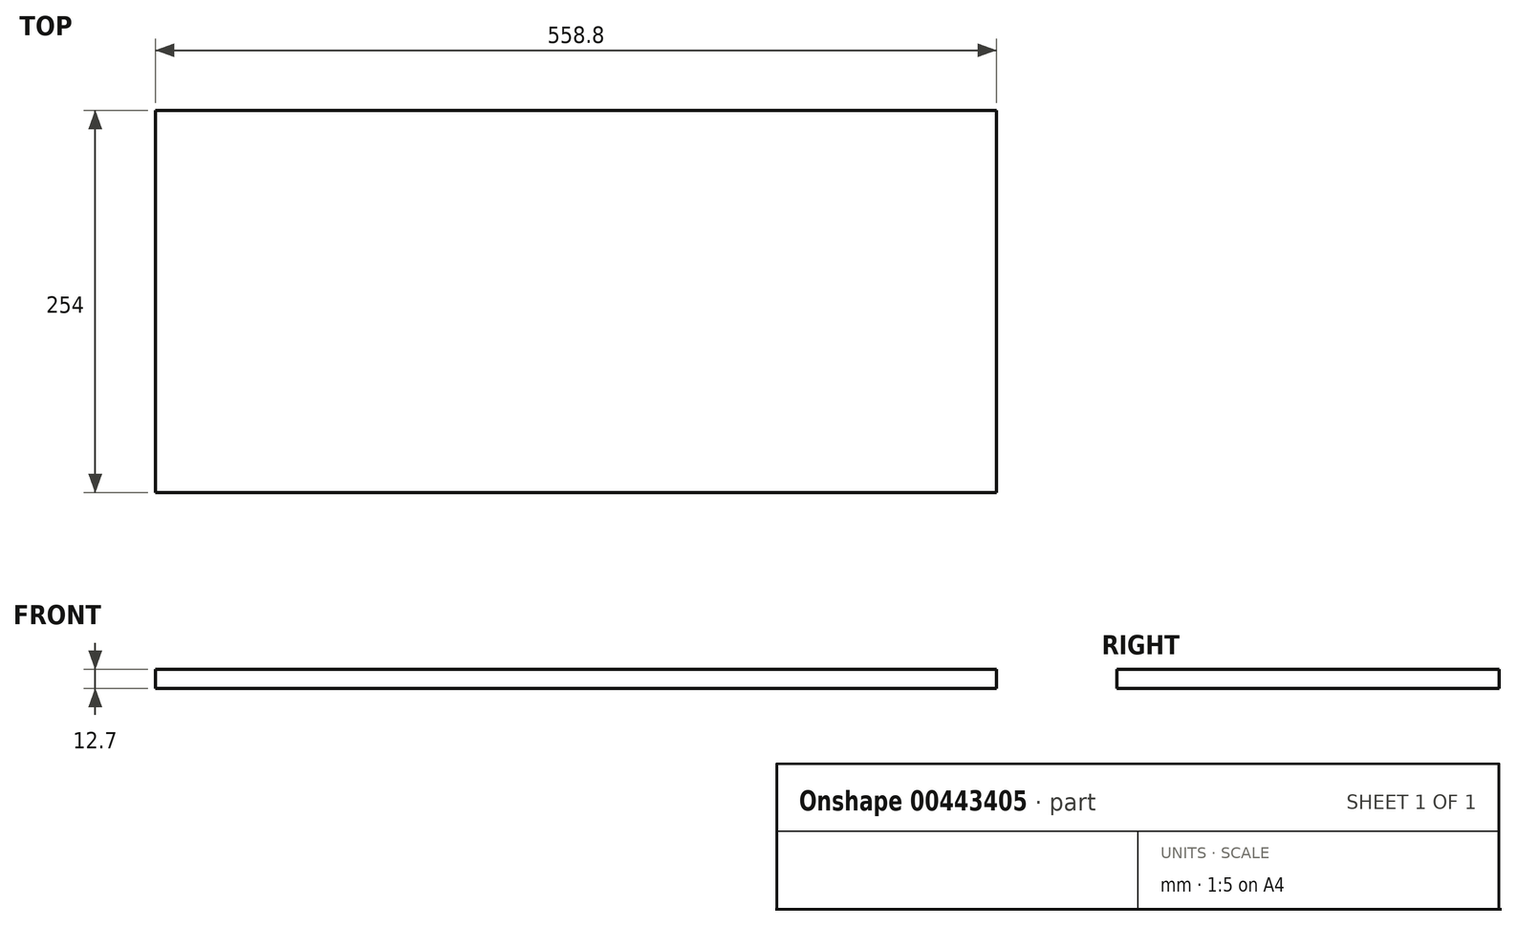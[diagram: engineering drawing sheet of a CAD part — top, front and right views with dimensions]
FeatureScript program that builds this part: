
annotation { "Feature Type Name" : "Feature", "Feature Type Description" : "" }
export const myFeature = defineFeature(function(context is Context, id is Id, definition is map)
    precondition{}
    {
        {
            var Q0;
            Q0=qCreatedBy(makeId("Top.planeOp"),FACE);
            var sketch = newSketch(context, id + "F0", { "sketchPlane" : qUnion([Q0])});
            skLineSegment(sketch, "E0.bottom", {"start": v(279.4, -127) * mm, "end": v(-279.4, -127) * mm});
            skLineSegment(sketch, "E0.top", {"start": v(279.4, 127) * mm, "end": v(-279.4, 127) * mm});
            skLineSegment(sketch, "E0.left", {"start": v(279.4, -127) * mm, "end": v(279.4, 127) * mm});
            skLineSegment(sketch, "E0.right", {"start": v(-279.4, -127) * mm, "end": v(-279.4, 127) * mm});
            skPoint(sketch, "E0.middle", {"position": v(0, 0) * mm});
            skSolve(sketch);
        }
        {
            var Q0;
            Q0 = qSketchRegion(id + "F0", true);
            extrude(context, id + "F1", {"entities" : qUnion([Q0]), "depth" : 12.7 * mm});
        }
    });
